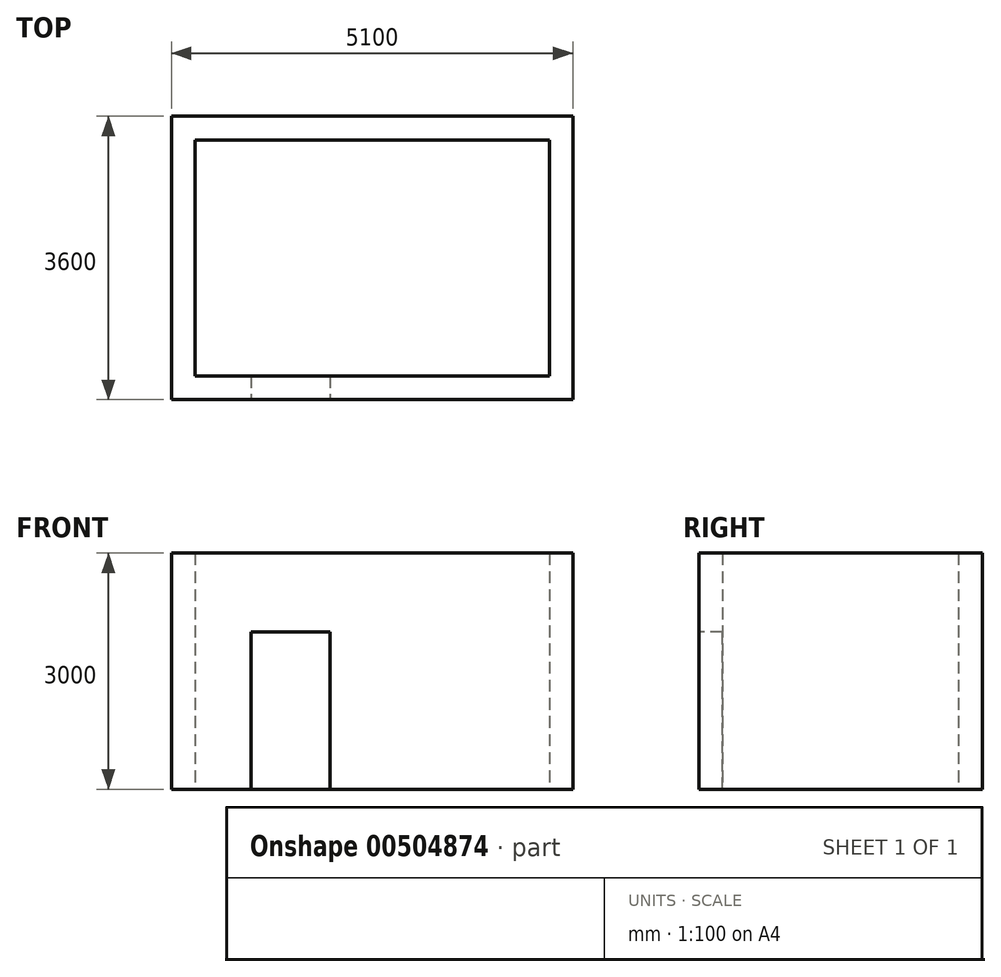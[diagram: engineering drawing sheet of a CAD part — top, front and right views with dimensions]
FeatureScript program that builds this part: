
annotation { "Feature Type Name" : "Feature", "Feature Type Description" : "" }
export const myFeature = defineFeature(function(context is Context, id is Id, definition is map)
    precondition{}
    {
        {
            var Q0;
            Q0=qCreatedBy(makeId("Top.planeOp"),FACE);
            var sketch = newSketch(context, id + "F0", { "sketchPlane" : qUnion([Q0])});
            skLineSegment(sketch, "E0", {"start": v(-2006.87, -1710.86) * mm, "end": v(2493.13, -1710.86) * mm});
            skLineSegment(sketch, "E1", {"start": v(2493.13, -1710.86) * mm, "end": v(2493.13, 1289.14) * mm});
            skLineSegment(sketch, "E2", {"start": v(2493.13, 1289.14) * mm, "end": v(-2006.87, 1289.14) * mm});
            skLineSegment(sketch, "E3", {"start": v(-2006.87, 1289.14) * mm, "end": v(-2006.87, -1710.86) * mm});
            skLineSegment(sketch, "E4.0", {"start": v(-2306.87, 1589.14) * mm, "end": v(-2306.87, -2010.86) * mm});
            skLineSegment(sketch, "E4.1", {"start": v(2793.13, 1589.14) * mm, "end": v(-2306.87, 1589.14) * mm});
            skLineSegment(sketch, "E4.2", {"start": v(2793.13, -2010.86) * mm, "end": v(2793.13, 1589.14) * mm});
            skLineSegment(sketch, "E4.3", {"start": v(-2306.87, -2010.86) * mm, "end": v(2793.13, -2010.86) * mm});
            skSolve(sketch);
        }
        {
            var Q0;
            Q0=makeQuery(id+"F0.imprint","IMPRINT",FACE,{"disambiguationData":[TD([[makeQuery(id+"F0.imprint","IMPRINT",EDGE,{"derivedFrom":sQuery(id+"F0.wireOp",EDGE,"E0")}),-1.0]])]});
            extrude(context, id + "F1", {"entities" : qUnion([Q0]), "depth" : 3000 * mm});
        }
        {
            var Q0;
            Q0=makeQuery(id+"F1.opExtrude","SWEPT_FACE",FACE,{"disambiguationData":[OSD([sQuery(id+"F0.wireOp",EDGE,"E4.3")])]});
            var sketch = newSketch(context, id + "F2", { "sketchPlane" : qUnion([Q0])});
            skLineSegment(sketch, "E5", {"start": v(-1293.31, 0) * mm, "end": v(-1293.31, 2000) * mm});
            skLineSegment(sketch, "E6", {"start": v(-1293.31, 2000) * mm, "end": v(-293.31, 2000) * mm});
            skLineSegment(sketch, "E7", {"start": v(-293.31, 2000) * mm, "end": v(-293.31, 0) * mm});
            skLineSegment(sketch, "E8", {"start": v(-293.31, 0) * mm, "end": v(-1293.31, 0) * mm});
            skSolve(sketch);
        }
        {
            var Q0;
            Q0 = qSketchRegion(id + "F2", true);
            var Q1;
            Q1=makeQuery(id+"F1.opExtrude","SWEPT_FACE",FACE,{"disambiguationData":[OSD([sQuery(id+"F0.wireOp",EDGE,"E0")])]});
            extrude(context, id + "F3", {"entities" : qUnion([Q0]), "operationType" : NewBodyOperationType.REMOVE, "endBound" : BoundingType.UP_TO_SURFACE, "oppositeDirection" : true, "endBoundEntityFace" : qUnion([Q1]), "depth" : 25 * mm});
        }
    });
